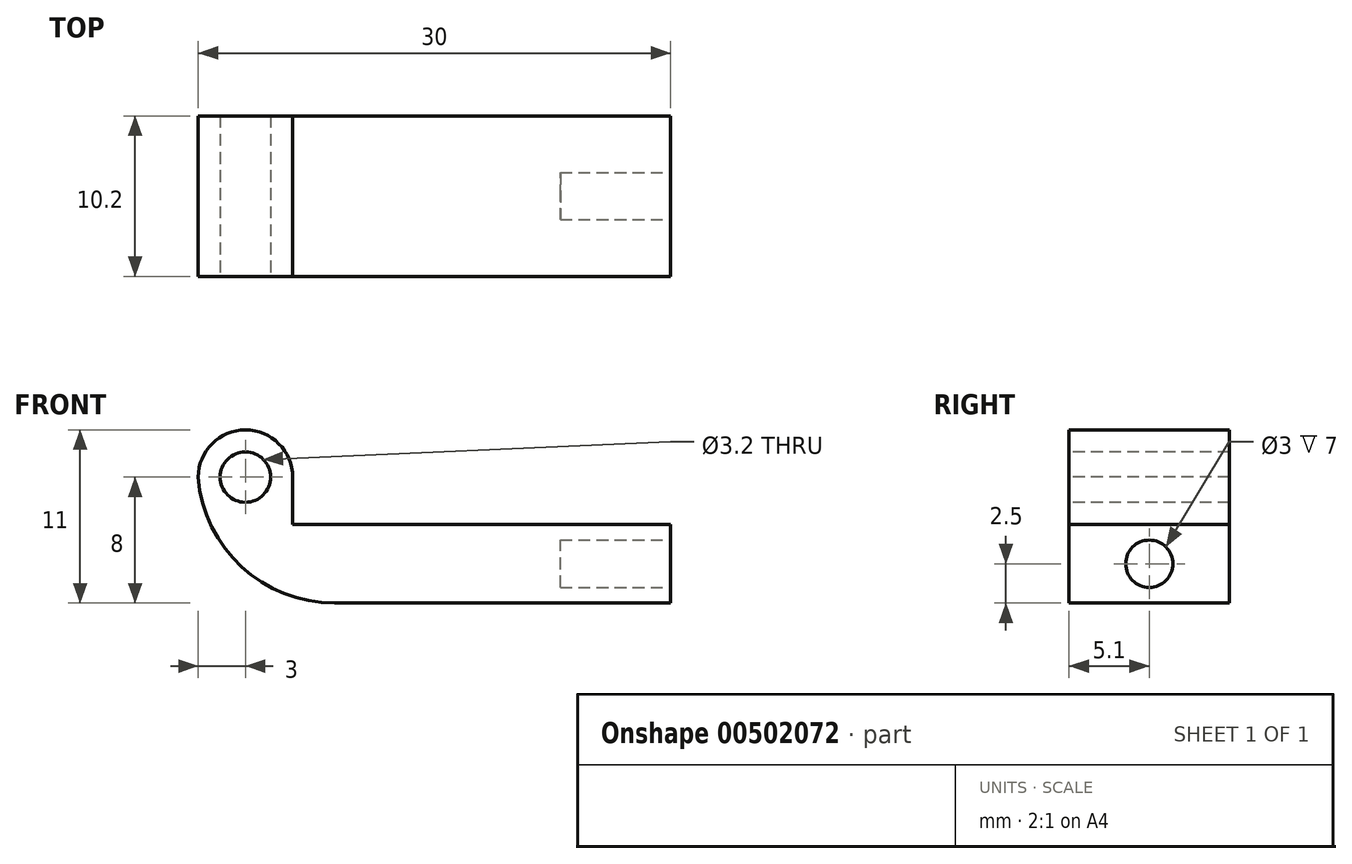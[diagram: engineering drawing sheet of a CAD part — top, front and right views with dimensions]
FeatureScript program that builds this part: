
annotation { "Feature Type Name" : "Feature", "Feature Type Description" : "" }
export const myFeature = defineFeature(function(context is Context, id is Id, definition is map)
    precondition{}
    {
        {
            var Q0;
            Q0=qCreatedBy(makeId("Top.planeOp"),FACE);
            var sketch = newSketch(context, id + "F0", { "sketchPlane" : qUnion([Q0])});
            skLineSegment(sketch, "E0.bottom", {"start": v(15, 5.1) * mm, "end": v(-15, 5.1) * mm});
            skLineSegment(sketch, "E0.top", {"start": v(15, -5.1) * mm, "end": v(-15, -5.1) * mm});
            skLineSegment(sketch, "E0.left", {"start": v(15, 5.1) * mm, "end": v(15, -5.1) * mm});
            skLineSegment(sketch, "E0.right", {"start": v(-15, 5.1) * mm, "end": v(-15, -5.1) * mm});
            skPoint(sketch, "E0.middle", {"position": v(0, 0) * mm});
            skLineSegment(sketch, "E1.bottom", {"start": v(3.5, 4.9) * mm, "end": v(11, 4.9) * mm});
            skLineSegment(sketch, "E1.top", {"start": v(3.5, -4.9) * mm, "end": v(11, -4.9) * mm});
            skLineSegment(sketch, "E1.left", {"start": v(3.5, 4.9) * mm, "end": v(3.5, -4.9) * mm});
            skLineSegment(sketch, "E1.right", {"start": v(11, 4.9) * mm, "end": v(11, -4.9) * mm});
            skLineSegment(sketch, "E2", {"start": v(15, 0) * mm, "end": v(11, 0) * mm, "construction": true});
            skPoint(sketch, "E3", {"position": v(11, 0) * mm});
            skSolve(sketch);
        }
        {
            var Q0;
            Q0=makeQuery(id+"F0.imprint","IMPRINT",FACE,{"disambiguationData":[TD([[makeQuery(id+"F0.imprint","IMPRINT",EDGE,{"derivedFrom":sQuery(id+"F0.wireOp",EDGE,"E0.bottom")}),1.0]])]});
            var Q1;
            Q1=makeQuery(id+"F0.imprint","IMPRINT",FACE,{"disambiguationData":[TD([[makeQuery(id+"F0.imprint","IMPRINT",EDGE,{"derivedFrom":sQuery(id+"F0.wireOp",EDGE,"E1.bottom")}),-1.0]])]});
            extrude(context, id + "F1", {"entities" : qUnion([Q0, Q1]), "depth" : 5 * mm});
        }
        {
            var Q0;
            Q0=makeQuery(id+"F1.opExtrude","CAP_FACE",FACE,{"disambiguationData":[OSD([sQuery(id+"F0.wireOp",EDGE,"E0.bottom"),sQuery(id+"F0.wireOp",EDGE,"E0.top"),sQuery(id+"F0.wireOp",EDGE,"E0.left"),sQuery(id+"F0.wireOp",EDGE,"E0.right"),sQuery(id+"F0.wireOp",EDGE,"E1.bottom"),sQuery(id+"F0.wireOp",EDGE,"E1.top"),sQuery(id+"F0.wireOp",EDGE,"E1.left"),sQuery(id+"F0.wireOp",EDGE,"E1.right")])],"isStart":false});
            var sketch = newSketch(context, id + "F2", { "sketchPlane" : qUnion([Q0])});
            skLineSegment(sketch, "E4.bottom", {"start": v(-15, 5.1) * mm, "end": v(-9, 5.1) * mm});
            skLineSegment(sketch, "E4.top", {"start": v(-15, -5.1) * mm, "end": v(-9, -5.1) * mm});
            skLineSegment(sketch, "E4.left", {"start": v(-15, 5.1) * mm, "end": v(-15, -5.1) * mm});
            skLineSegment(sketch, "E4.right", {"start": v(-9, 5.1) * mm, "end": v(-9, -5.1) * mm});
            skSolve(sketch);
        }
        {
            var Q0;
            Q0 = qSketchRegion(id + "F2", true);
            extrude(context, id + "F3", {"entities" : qUnion([Q0]), "operationType" : NewBodyOperationType.ADD, "depth" : 6 * mm});
        }
        {
            var Q0;
            Q0=makeQuery(id+"F3.boolean.opBoolean","MERGE",FACE,{"derivedFrom":[makeQuery(id+"F1.opExtrude","SWEPT_FACE",FACE,{"disambiguationData":[OSD([sQuery(id+"F0.wireOp",EDGE,"E0.top")])]}),makeQuery(id+"F3.opExtrude","SWEPT_FACE",FACE,{"disambiguationData":[OSD([sQuery(id+"F2.wireOp",EDGE,"E4.top")])]})]});
            var sketch = newSketch(context, id + "F4", { "sketchPlane" : qUnion([Q0])});
            skPoint(sketch, "E5", {"position": v(-12, 8) * mm});
            skPoint(sketch, "E5.positionSnap0", {"position": v(-9, 8) * mm});
            skPoint(sketch, "E5.positionSnap1", {"position": v(-12, 11) * mm});
            skCircle(sketch, "E6", {"center": v(-12, 8) * mm, "radius": 1.6 * mm});
            skSolve(sketch);
        }
        {
            var Q0;
            Q0=makeQuery(id+"F4.imprint","IMPRINT",FACE,{"disambiguationData":[TD([[makeQuery(id+"F4.imprint","IMPRINT",EDGE,{"derivedFrom":sQuery(id+"F4.wireOp",EDGE,"E6")}),1.0]])]});
            extrude(context, id + "F5", {"entities" : qUnion([Q0]), "operationType" : NewBodyOperationType.REMOVE, "oppositeDirection" : true, "depth" : 25 * mm});
        }
        {
            var Q0;
            Q0=makeQuery(id+"F3.opExtrude","CAP_EDGE",EDGE,{"disambiguationData":[OSD([sQuery(id+"F2.wireOp",EDGE,"E4.right")])],"isStart":false});
            var Q1;
            Q1=makeQuery(id+"F3.opExtrude","CAP_EDGE",EDGE,{"disambiguationData":[OSD([sQuery(id+"F2.wireOp",EDGE,"E4.left")])],"isStart":false});
            fillet(context, id + "F6", {"entities" : qUnion([Q0, Q1]), "radius" : 3 * mm, "tangentPropagation" : true, "allowEdgeOverflow" : false});
        }
        {
            var Q0;
            Q0=makeQuery(id+"F1.opExtrude","CAP_EDGE",EDGE,{"disambiguationData":[OSD([sQuery(id+"F0.wireOp",EDGE,"E0.right")])],"isStart":true});
            fillet(context, id + "F7", {"entities" : qUnion([Q0]), "radius" : 8.7 * mm, "tangentPropagation" : true, "allowEdgeOverflow" : false});
        }
        {
            var Q0;
            Q0=makeQuery(id+"F1.opExtrude","SWEPT_FACE",FACE,{"disambiguationData":[OSD([sQuery(id+"F0.wireOp",EDGE,"E0.left")])]});
            var sketch = newSketch(context, id + "F8", { "sketchPlane" : qUnion([Q0])});
            skPoint(sketch, "E7", {"position": v(0, 2.5) * mm});
            skPoint(sketch, "E7.positionSnap0", {"position": v(5.1, 2.5) * mm});
            skCircle(sketch, "E8", {"center": v(0, 2.5) * mm, "radius": 1.5 * mm});
            skCircle(sketch, "E9", {"center": v(0, 2.5) * mm, "radius": 5 * mm});
            skSolve(sketch);
        }
        {
            var Q0;
            Q0=makeQuery(id+"F8.imprint","IMPRINT",FACE,{"disambiguationData":[TD([[makeQuery(id+"F8.imprint","IMPRINT",EDGE,{"derivedFrom":sQuery(id+"F8.wireOp",EDGE,"E8")}),1.0]])]});
            extrude(context, id + "F9", {"entities" : qUnion([Q0]), "operationType" : NewBodyOperationType.REMOVE, "oppositeDirection" : true, "depth" : 7 * mm});
        }
    });
